# Revit family: DC_Holyoake_BackDraftDamper_BDE_Channel_12
name_source: partatom
category: Air Terminals
revit_build: Autodesk Revit 2013 (Build: 20120221_2030(x64)
units: mm (PartAtom-declared; Revit-internal decimal feet)

## types (1)
- BDE Channel
    Air Stream Height = 518 mm  [stored 1.69948 ft]
    Air Stream Width = 568 mm  [stored 1.86352 ft]
    Blade ArrayNumber = 6
    Blade Count = 5
    Blade Cut Setout = 435.15 mm
    Blade Length = 552 mm  [stored 1.81102 ft]
    Blade Pitch = 87.03 mm  [stored 0.285531 ft]
    Channel Width = 16 mm  [stored 0.0524934 ft]
    Damper Depth = 50.75 mm  [stored 0.166503 ft]
    Exact Overall Height = 550 mm
    Exact Overall Width = 600 mm  [stored 1.9685 ft]
    Louvre Offset = 500 mm  [stored 1.64042 ft]
    Manufacturer = Holyoake Industries Ltd
    Max Flow = 10.0 L/s
    Maximum Size = 1000 W * 11140 H
    Min Flow = 100.0 L/s
    Minimum Size = 150 * 150
    Model = BDE Channel
    Nominal Height = 556 mm  [stored 1.82415 ft]
    Nominal Width = 606 mm  [stored 1.98819 ft]
    Static Pressure Max = 0.0 Pa
    Static Pressure Min = 0.0 Pa
    Technical Data = http://www.productspec.net
    Top Blade Height = 66.85 mm
    Type Comments = Back Draft Damper
    URL = http://www.productspec.net

note: [stored X ft] marks values corroborated as IEEE doubles in the binary element streams (Revit-internal decimal feet)

## geometry (parser evidence)
native form markers: Sweep x10
no freeform markers — native parametric forms only
